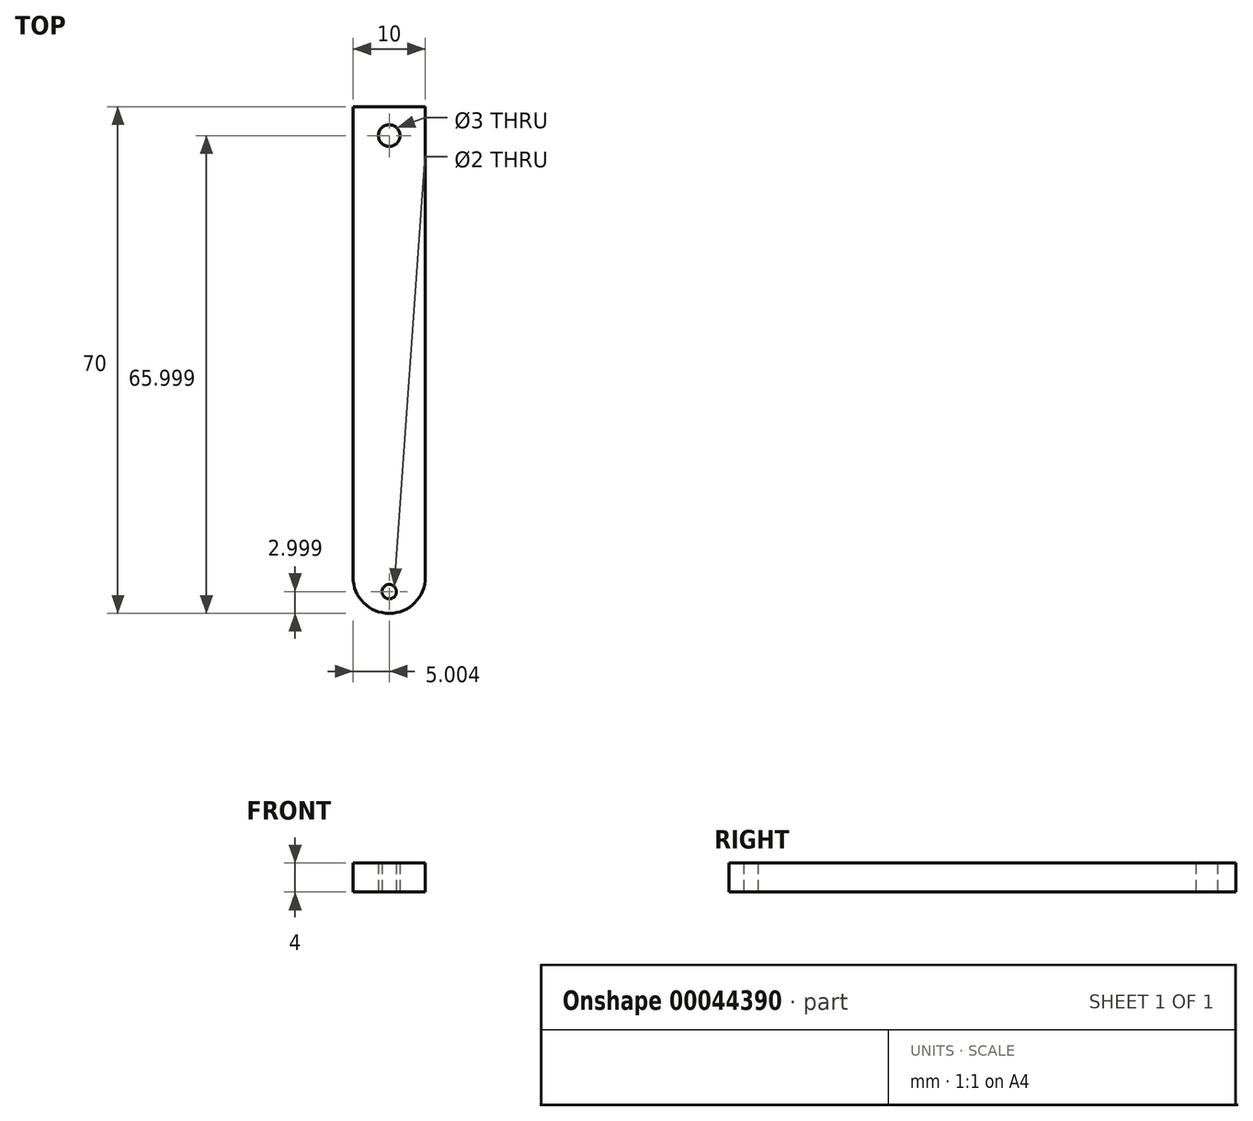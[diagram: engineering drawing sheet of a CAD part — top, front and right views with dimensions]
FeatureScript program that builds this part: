
annotation { "Feature Type Name" : "Feature", "Feature Type Description" : "" }
export const myFeature = defineFeature(function(context is Context, id is Id, definition is map)
    precondition{}
    {
        {
            var Q0;
            Q0=qCreatedBy(makeId("Top.planeOp"),FACE);
            var sketch = newSketch(context, id + "F0", { "sketchPlane" : qUnion([Q0])});
            skLineSegment(sketch, "E0.bottom", {"start": v(-323.12, 44.46) * mm, "end": v(-313.12, 44.46) * mm});
            skLineSegment(sketch, "E0.left", {"start": v(-323.12, 44.46) * mm, "end": v(-323.12, -20.54) * mm});
            skLineSegment(sketch, "E0.right", {"start": v(-313.12, 44.46) * mm, "end": v(-313.12, -20.54) * mm});
            skLineSegment(sketch, "E1", {"start": v(-313.12, 44.46) * mm, "end": v(-313.12, 36.46) * mm});
            skLineSegment(sketch, "E2", {"start": v(-313.12, 36.46) * mm, "end": v(-323.12, 36.46) * mm, "construction": true});
            skLineSegment(sketch, "E3", {"start": v(-313.12, 36.46) * mm, "end": v(-313.12, -20.54) * mm});
            skCircle(sketch, "E4", {"center": v(-318.12, 40.46) * mm, "radius": 1.5 * mm});
            skArc(sketch, "E5", {"start": v(-323.12, -20.54) * mm, "mid": v(-321.65, -24.08) * mm, "end": v(-318.12, -25.54) * mm});
            skArc(sketch, "E6", {"start": v(-318.12, -25.54) * mm, "mid": v(-314.58, -24.08) * mm, "end": v(-313.12, -20.54) * mm});
            skLineSegment(sketch, "E7", {"start": v(-265.74, -25.54) * mm, "end": v(-265.74, 44.46) * mm, "construction": true});
            skLineSegment(sketch, "E8", {"start": v(-318.12, -25.54) * mm, "end": v(-318.12, -22.54) * mm, "construction": true});
            skCircle(sketch, "E9", {"center": v(-318.12, -22.54) * mm, "radius": 1 * mm});
            skSolve(sketch);
        }
        {
            var Q0;
            Q0=makeQuery(id+"F0.imprint","IMPRINT",FACE,{"disambiguationData":[TD([[makeQuery(id+"F0.imprint","IMPRINT",EDGE,{"derivedFrom":sQuery(id+"F0.wireOp",EDGE,"E0.bottom")}),-1.0]])]});
            extrude(context, id + "F1", {"entities" : qUnion([Q0]), "depth" : 4 * mm});
        }
    });
